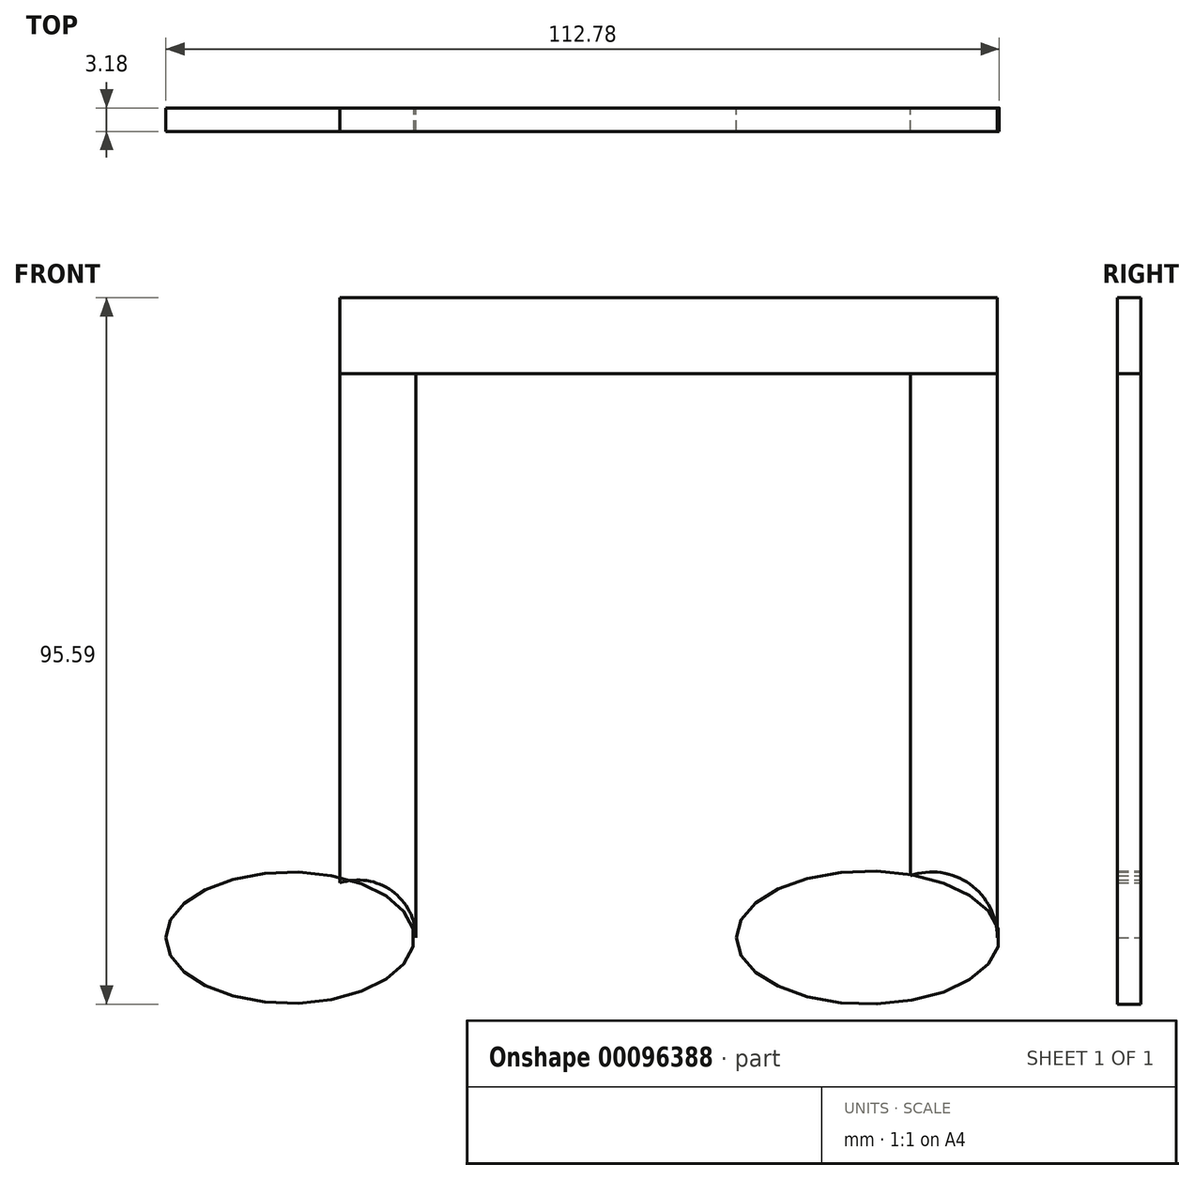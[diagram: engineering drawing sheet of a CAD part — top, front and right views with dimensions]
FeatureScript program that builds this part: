
annotation { "Feature Type Name" : "Feature", "Feature Type Description" : "" }
export const myFeature = defineFeature(function(context is Context, id is Id, definition is map)
    precondition{}
    {
        {
            var Q0;
            Q0=qCreatedBy(makeId("Front.planeOp"),FACE);
            var sketch = newSketch(context, id + "F0", { "sketchPlane" : qUnion([Q0])});
            skEllipse(sketch, "E0", {"center": v(-40.35, 0) * mm, "majorRadius": 16.8 * mm, "minorRadius": 8.9 * mm, "majorAxis": v(-1, 0)});
            skSolve(sketch);
        }
        {
            var Q0;
            Q0=qCreatedBy(makeId("Front.planeOp"),FACE);
            var sketch = newSketch(context, id + "F1", { "sketchPlane" : qUnion([Q0])});
            skEllipse(sketch, "E1", {"center": v(37.85, 0) * mm, "majorRadius": 17.8 * mm, "minorRadius": 9 * mm, "majorAxis": v(-1, 0)});
            skSolve(sketch);
        }
        {
            var Q0;
            Q0=qCreatedBy(makeId("Front.planeOp"),FACE);
            var sketch = newSketch(context, id + "F2", { "sketchPlane" : qUnion([Q0])});
            skLineSegment(sketch, "E2", {"start": v(-23.3, 0) * mm, "end": v(-23.3, 76.32) * mm});
            skLineSegment(sketch, "E3", {"start": v(-23.3, 76.32) * mm, "end": v(-33.58, 76.32) * mm});
            skLineSegment(sketch, "E4", {"start": v(-33.58, 76.32) * mm, "end": v(-33.58, 7.4) * mm});
            skArc(sketch, "E5", {"start": v(-23.3, 0) * mm, "mid": v(-26.55, 6.33) * mm, "end": v(-33.58, 7.4) * mm});
            skSolve(sketch);
        }
        {
            var Q0;
            Q0=qCreatedBy(makeId("Front.planeOp"),FACE);
            var sketch = newSketch(context, id + "F3", { "sketchPlane" : qUnion([Q0])});
            skLineSegment(sketch, "E6", {"start": v(55.4, 0) * mm, "end": v(55.4, 76.32) * mm});
            skLineSegment(sketch, "E7", {"start": v(55.4, 76.32) * mm, "end": v(43.61, 76.32) * mm});
            skLineSegment(sketch, "E8", {"start": v(43.61, 76.32) * mm, "end": v(43.61, 8.4) * mm});
            skArc(sketch, "E9", {"start": v(55.4, 0) * mm, "mid": v(51.66, 7.23) * mm, "end": v(43.61, 8.4) * mm});
            skSolve(sketch);
        }
        {
            var Q0;
            Q0=qCreatedBy(makeId("Front.planeOp"),FACE);
            var sketch = newSketch(context, id + "F4", { "sketchPlane" : qUnion([Q0])});
            skLineSegment(sketch, "E10", {"start": v(-33.58, 76.32) * mm, "end": v(55.4, 76.32) * mm});
            skLineSegment(sketch, "E11", {"start": v(55.4, 76.32) * mm, "end": v(55.4, 86.6) * mm});
            skLineSegment(sketch, "E12", {"start": v(55.4, 86.6) * mm, "end": v(-33.58, 86.6) * mm});
            skLineSegment(sketch, "E13", {"start": v(-33.58, 86.6) * mm, "end": v(-33.58, 76.32) * mm});
            skSolve(sketch);
        }
        {
            var Q0;
            Q0=makeQuery(id+"F0.imprint","IMPRINT",FACE,{"disambiguationData":[TD([[makeQuery(id+"F0.imprint","IMPRINT",EDGE,{"derivedFrom":sQuery(id+"F0.wireOp",EDGE,"E0")}),1.0]])]});
            var Q1;
            Q1=makeQuery(id+"F1.imprint","IMPRINT",FACE,{"disambiguationData":[TD([[makeQuery(id+"F1.imprint","IMPRINT",EDGE,{"derivedFrom":sQuery(id+"F1.wireOp",EDGE,"E1")}),1.0]])]});
            var Q2;
            Q2=makeQuery(id+"F2.imprint","IMPRINT",FACE,{"disambiguationData":[TD([[makeQuery(id+"F2.imprint","IMPRINT",EDGE,{"derivedFrom":sQuery(id+"F2.wireOp",EDGE,"E2")}),1.0]])]});
            var Q3;
            Q3=makeQuery(id+"F3.imprint","IMPRINT",FACE,{"disambiguationData":[TD([[makeQuery(id+"F3.imprint","IMPRINT",EDGE,{"derivedFrom":sQuery(id+"F3.wireOp",EDGE,"E6")}),1.0]])]});
            var Q4;
            Q4=makeQuery(id+"F4.imprint","IMPRINT",FACE,{"disambiguationData":[TD([[makeQuery(id+"F4.imprint","IMPRINT",EDGE,{"derivedFrom":sQuery(id+"F4.wireOp",EDGE,"E10")}),1.0]])]});
            extrude(context, id + "F5", {"entities" : qUnion([Q0, Q1, Q2, Q3, Q4]), "endBound" : BoundingType.SYMMETRIC, "depth" : 3.17 * mm});
        }
    });
